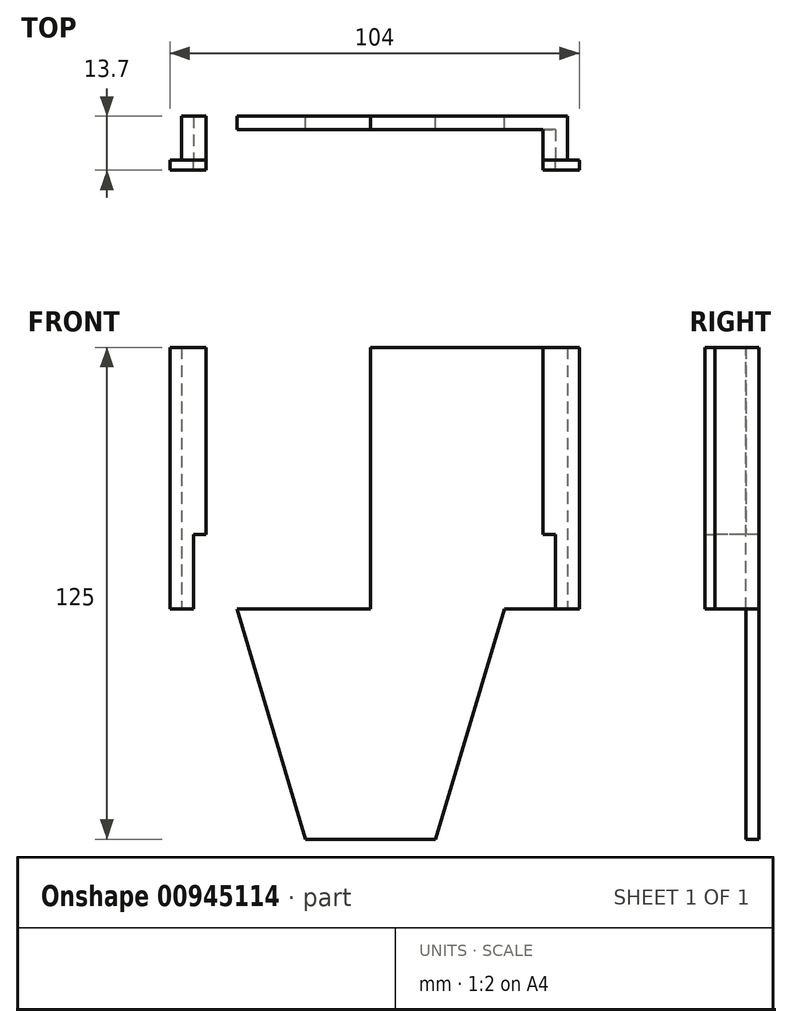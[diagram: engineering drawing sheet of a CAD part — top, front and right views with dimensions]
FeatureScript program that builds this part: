
annotation { "Feature Type Name" : "Feature", "Feature Type Description" : "" }
export const myFeature = defineFeature(function(context is Context, id is Id, definition is map)
    precondition{}
    {
        {
            var Q0;
            Q0=qCreatedBy(makeId("Front.planeOp"),FACE);
            var sketch = newSketch(context, id + "F0", { "sketchPlane" : qUnion([Q0])});
            skLineSegment(sketch, "E0.bottom", {"start": v(-108.76, 19) * mm, "end": v(-4.76, 19) * mm});
            skLineSegment(sketch, "E0.top", {"start": v(-108.76, -47.5) * mm, "end": v(-4.76, -47.5) * mm});
            skLineSegment(sketch, "E0.left", {"start": v(-108.76, 19) * mm, "end": v(-108.76, -47.5) * mm});
            skLineSegment(sketch, "E0.right", {"start": v(-4.76, 19) * mm, "end": v(-4.76, -47.5) * mm});
            skLineSegment(sketch, "E1", {"start": v(-4.76, -47.5) * mm, "end": v(-56.76, -47.5) * mm});
            skLineSegment(sketch, "E2", {"start": v(-56.76, -47.5) * mm, "end": v(-56.76, 19) * mm});
            skLineSegment(sketch, "E3", {"start": v(-56.76, 19) * mm, "end": v(-13.5, 19) * mm});
            skLineSegment(sketch, "E4", {"start": v(-13.5, 19) * mm, "end": v(-99.5, 19) * mm});
            skLineSegment(sketch, "E5", {"start": v(-99.5, -47.5) * mm, "end": v(-102.76, -47.5) * mm});
            skLineSegment(sketch, "E6", {"start": v(-102.76, -47.5) * mm, "end": v(-102.76, -28.5) * mm});
            skLineSegment(sketch, "E7", {"start": v(-102.76, -28.5) * mm, "end": v(-99.5, -28.5) * mm});
            skLineSegment(sketch, "E8.MirrorCS", {"start": v(-10.76, -47.5) * mm, "end": v(-10.76, -28.5) * mm});
            skLineSegment(sketch, "E9.MirrorCS", {"start": v(-10.76, -28.5) * mm, "end": v(-14, -28.5) * mm});
            skLineSegment(sketch, "E10", {"start": v(-108.76, 19) * mm, "end": v(-105.76, 19) * mm});
            skLineSegment(sketch, "E11", {"start": v(-105.76, 19) * mm, "end": v(-105.76, -47.5) * mm});
            skLineSegment(sketch, "E12.MirrorCS", {"start": v(-7.76, 19) * mm, "end": v(-7.76, -47.5) * mm});
            skLineSegment(sketch, "E13", {"start": v(-99.5, 19) * mm, "end": v(-99.5, -47.5) * mm});
            skLineSegment(sketch, "E14.MirrorCS", {"start": v(-14, 19) * mm, "end": v(-14, -47.5) * mm});
            skSolve(sketch);
        }
        {
            var Q0;
            {var subQ0=sQuery(id+"F0.wireOp",EDGE,"E0.left");Q0=makeQuery(id+"F0.imprint","IMPRINT",FACE,{"disambiguationData":[TD([[makeQuery(id+"F0.imprint","IMPRINT",EDGE,{"derivedFrom":subQ0}),1.0]])]});}
            var Q1;
            {var subQ0=sQuery(id+"F0.wireOp",EDGE,"E0.right");Q1=makeQuery(id+"F0.imprint","IMPRINT",FACE,{"disambiguationData":[TD([[makeQuery(id+"F0.imprint","IMPRINT",EDGE,{"derivedFrom":subQ0}),-1.0]])]});}
            var Q2;
            {var subQ0=sQuery(id+"F0.wireOp",EDGE,"E6");Q2=makeQuery(id+"F0.imprint","IMPRINT",FACE,{"disambiguationData":[TD([[makeQuery(id+"F0.imprint","IMPRINT",EDGE,{"derivedFrom":subQ0}),1.0]])]});}
            var Q3;
            {var subQ0=sQuery(id+"F0.wireOp",EDGE,"E8.MirrorCS");Q3=makeQuery(id+"F0.imprint","IMPRINT",FACE,{"disambiguationData":[TD([[makeQuery(id+"F0.imprint","IMPRINT",EDGE,{"derivedFrom":subQ0}),-1.0]])]});}
            extrude(context, id + "F1", {"entities" : qUnion([Q0, Q1, Q2, Q3]), "depth" : 2.5 * mm, "offsetDistance" : 25 * mm});
        }
        {
            var Q0;
            {var subQ0=sQuery(id+"F0.wireOp",EDGE,"E6");Q0=makeQuery(id+"F0.imprint","IMPRINT",FACE,{"disambiguationData":[TD([[makeQuery(id+"F0.imprint","IMPRINT",EDGE,{"derivedFrom":subQ0}),1.0]])]});}
            var Q1;
            {var subQ0=sQuery(id+"F0.wireOp",EDGE,"E8.MirrorCS");Q1=makeQuery(id+"F0.imprint","IMPRINT",FACE,{"disambiguationData":[TD([[makeQuery(id+"F0.imprint","IMPRINT",EDGE,{"derivedFrom":subQ0}),-1.0]])]});}
            extrude(context, id + "F2", {"entities" : qUnion([Q0, Q1]), "oppositeDirection" : true, "depth" : 11.2 * mm, "offsetDistance" : 25 * mm});
        }
        {
            var Q0;
            Q0=makeQuery(id+"F2.opExtrude","CAP_FACE",FACE,{"disambiguationData":[OSD([sQuery(id+"F0.wireOp",EDGE,"E0.bottom"),sQuery(id+"F0.wireOp",EDGE,"E0.top"),sQuery(id+"F0.wireOp",EDGE,"VHu2uuCE-mhUQ-FtHU-AAhZ-2lJ3eGuVZ54X"),sQuery(id+"F0.wireOp",EDGE,"E6"),sQuery(id+"F0.wireOp",EDGE,"E7"),sQuery(id+"F0.wireOp",EDGE,"E11")])],"isStart":false});
            var sketch = newSketch(context, id + "F3", { "sketchPlane" : qUnion([Q0])});
            skLineSegment(sketch, "E15.bottom", {"start": v(105.76, -47.5) * mm, "end": v(9.76, -47.5) * mm});
            skLineSegment(sketch, "E15.top", {"start": v(105.76, 19) * mm, "end": v(9.76, 19) * mm});
            skLineSegment(sketch, "E15.left", {"start": v(105.76, -47.5) * mm, "end": v(105.76, 19) * mm});
            skLineSegment(sketch, "E15.right", {"start": v(9.76, -47.5) * mm, "end": v(9.76, 19) * mm});
            skLineSegment(sketch, "E16", {"start": v(57.76, -47.5) * mm, "end": v(57.76, 19) * mm});
            skLineSegment(sketch, "E17", {"start": v(57.76, 19) * mm, "end": v(57.76, -106) * mm});
            skLineSegment(sketch, "E18", {"start": v(57.76, -106) * mm, "end": v(41.26, -106) * mm});
            skLineSegment(sketch, "E19.MirrorCS", {"start": v(57.76, -106) * mm, "end": v(74.26, -106) * mm});
            skLineSegment(sketch, "E20", {"start": v(57.76, -47.5) * mm, "end": v(91.76, -47.5) * mm});
            skLineSegment(sketch, "E21.MirrorCS", {"start": v(57.76, -47.5) * mm, "end": v(23.76, -47.5) * mm});
            skLineSegment(sketch, "E22", {"start": v(91.76, -47.5) * mm, "end": v(74.26, -106) * mm});
            skLineSegment(sketch, "E23.MirrorCS", {"start": v(23.76, -47.5) * mm, "end": v(41.26, -106) * mm});
            skSolve(sketch);
        }
        {
            var Q0;
            {var subQ0=sQuery(id+"F3.wireOp",EDGE,"E20");Q0=makeQuery(id+"F3.imprint","IMPRINT",FACE,{"disambiguationData":[TD([[makeQuery(id+"F3.imprint","IMPRINT",EDGE,{"derivedFrom":subQ0}),1.0]])]});}
            var Q1;
            {var subQ0=sQuery(id+"F3.wireOp",EDGE,"E19.MirrorCS");Q1=makeQuery(id+"F3.imprint","IMPRINT",FACE,{"disambiguationData":[TD([[makeQuery(id+"F3.imprint","IMPRINT",EDGE,{"derivedFrom":subQ0}),1.0]])]});}
            var Q2;
            {var subQ0=sQuery(id+"F3.wireOp",EDGE,"E18");Q2=makeQuery(id+"F3.imprint","IMPRINT",FACE,{"disambiguationData":[TD([[makeQuery(id+"F3.imprint","IMPRINT",EDGE,{"derivedFrom":subQ0}),-1.0]])]});}
            var Q3;
            {var subQ4=sQuery(id+"F3.wireOp",EDGE,"E15.right");Q3=makeQuery(id+"F3.imprint","IMPRINT",FACE,{"disambiguationData":[TD([[makeQuery(id+"F3.imprint","IMPRINT",EDGE,{"derivedFrom":subQ4}),-1.0]])]});}
            extrude(context, id + "F4", {"entities" : qUnion([Q0, Q1, Q2, Q3]), "operationType" : NewBodyOperationType.ADD, "oppositeDirection" : true, "depth" : 3.35 * mm, "offsetDistance" : 25 * mm});
        }
    });
